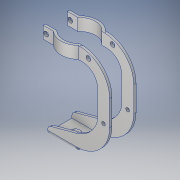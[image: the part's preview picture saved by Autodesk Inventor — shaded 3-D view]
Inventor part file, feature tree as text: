
AUTODESK INVENTOR PART (.ipt)
format: ipt  version: 2018 (Build 220112000, 112)  size: 323,072 bytes
history: native  units: in
note: dims shown in document units (in); Inventor stores cm internally (conversion verified against a paired STEP export)
features: extrude x10, sketch x10, fillet x5
ambient origin geometry x8: Origin, YZ Plane, XZ Plane, XY Plane, X Axis, Y Axis, Z Axis, Center Point
bodies: Solid1 (feature_tree)
feature tree (25):
  extrude  "Extrusion1"  Depth=0.438in
  extrude  "Extrusion2"  Depth=0.237in
  extrude  "Extrusion3"  Depth=0.0385in TaperAngle=0.0deg
  fillet  "Fillet1"  Radius=0.0385in
  fillet  "Fillet2"  Radius=0.0385in
  extrude  "Extrusion4"  TaperAngle=15.0deg  [1 undecoded]
  extrude  "Extrusion5"  Depth=0.0625in
  extrude  "Extrusion6"  Depth=0.0625in TaperAngle=0.0deg
  fillet  "Fillet3"  Radius=1.275in
  extrude  "Extrusion7"  Depth=0.5in
  fillet  "Fillet4"  Radius=0.2in
  fillet  "Fillet5"  Radius=0.5in
  extrude  "Extrusion11"  Depth=0.0625in
  extrude  "Extrusion10"  Depth=0.2in
  extrude  "Extrusion12"  Depth=0.25in
  sketch  "Sketch1"  dims[d0=0.4735in d1=0.438in]
  sketch  "Sketch2"  dims[d2=0.219in d3=0.237in]
  sketch  "Sketch3"  dims[d4=0.1565in d5=0.038in d6=0.0in d7=0.0385in d8=0.0385in]
  sketch  "Sketch4"  dims[d9=0.5in d10=0.0in d11=15.0deg]
  sketch  "Sketch5"  dims[d12=0.5in d13=0.0in d14=0.0625in]
  sketch  "Sketch6"  dims[d15=0.0625in d16=0.55in d17=0.0in d18=1.275in d19=0.0in]
  sketch  "Sketch7"  dims[d20=135.0deg d21=0.55in d22=0.2in d23=0.5in]
  sketch  "Sketch10"  dims[d24=1.275in d25=0.0in d26=0.0625in]
  sketch  "Sketch11"  dims[d27=0.2in d28=0.2in]
  sketch  "Sketch12"  dims[d29=0.9in d30=0.0in d31=0.25in d32=0.5in d45=0.05in d46=0.1in d47=0.1in d48=0.15in d49=0.1in d50=0.0in d51=0.078in d52=0.078in d53=0.06in d54=0.2in d55=0.0in d56=0.375in d57=0.225in d58=0.53in d59=0.0385in d60=0.039in d61=0.2in d62=0.0in d63=0.375in d64=0.225in d65=0.2in d66=0.0in]
note: 1 required parameter value undecoded (feature->parameter linkage not recoverable at this tier; creation-order binding heuristic only, values carry confidence <= 0.55)
